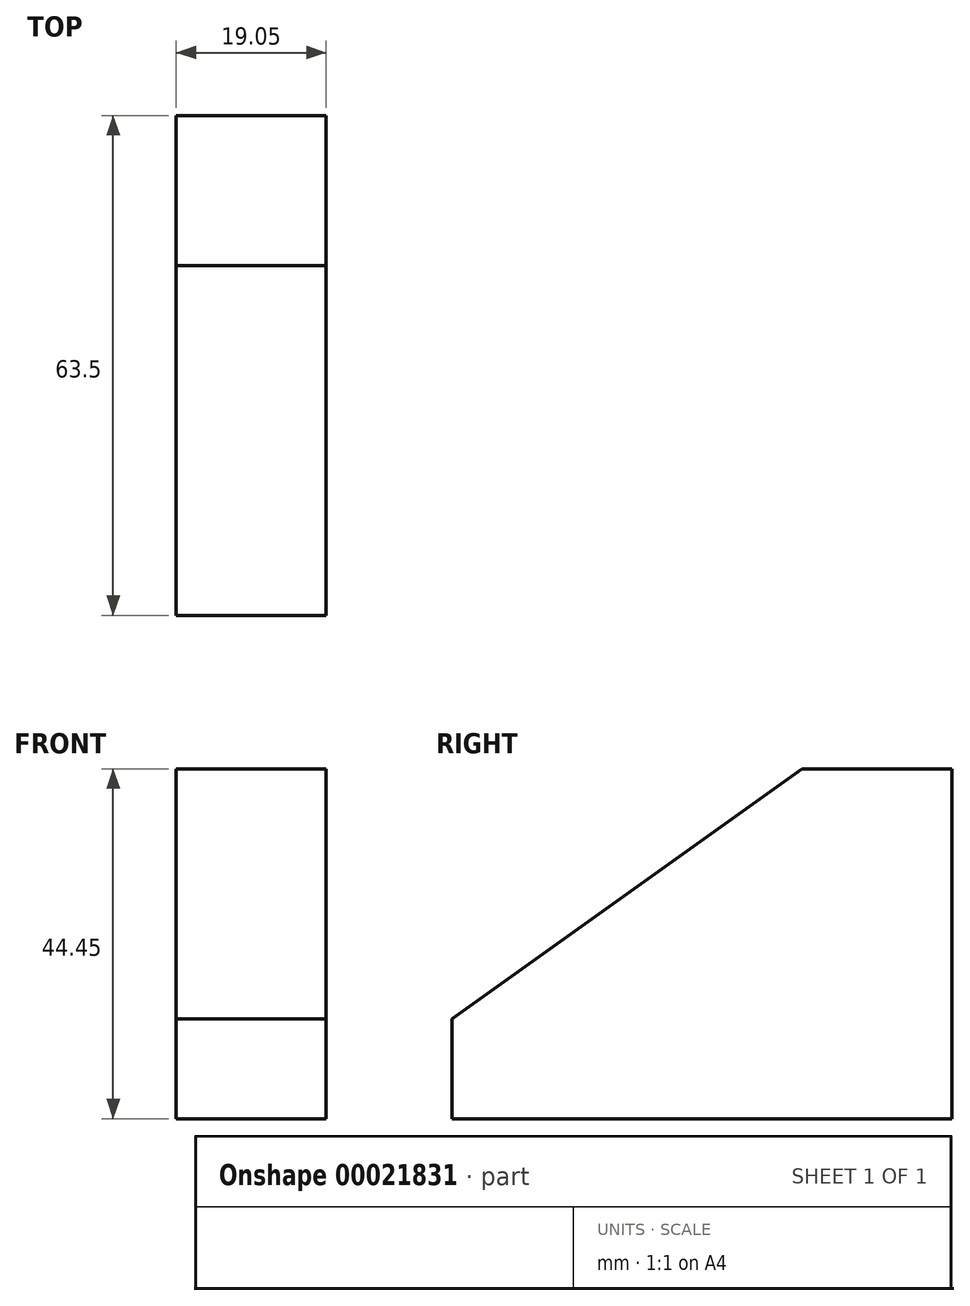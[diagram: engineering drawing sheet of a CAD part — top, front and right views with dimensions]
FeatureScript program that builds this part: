
annotation { "Feature Type Name" : "Feature", "Feature Type Description" : "" }
export const myFeature = defineFeature(function(context is Context, id is Id, definition is map)
    precondition{}
    {
        {
            var Q0;
            Q0=qCreatedBy(makeId("Right.planeOp"),FACE);
            var sketch = newSketch(context, id + "F0", { "sketchPlane" : qUnion([Q0])});
            skLineSegment(sketch, "E0.bottom", {"start": v(51.75, 10.08) * mm, "end": v(70.8, 10.08) * mm});
            skLineSegment(sketch, "E0.top", {"start": v(7.3, -34.37) * mm, "end": v(70.8, -34.37) * mm});
            skLineSegment(sketch, "E0.left", {"start": v(7.3, -21.67) * mm, "end": v(7.3, -34.37) * mm});
            skLineSegment(sketch, "E0.right", {"start": v(70.8, 10.08) * mm, "end": v(70.8, -34.37) * mm});
            skLineSegment(sketch, "E1", {"start": v(51.75, 10.08) * mm, "end": v(7.3, -21.67) * mm});
            skSolve(sketch);
        }
        {
            var Q0;
            Q0 = qSketchRegion(id + "F0", true);
            extrude(context, id + "F1", {"entities" : qUnion([Q0]), "depth" : 19.05 * mm});
        }
    });
